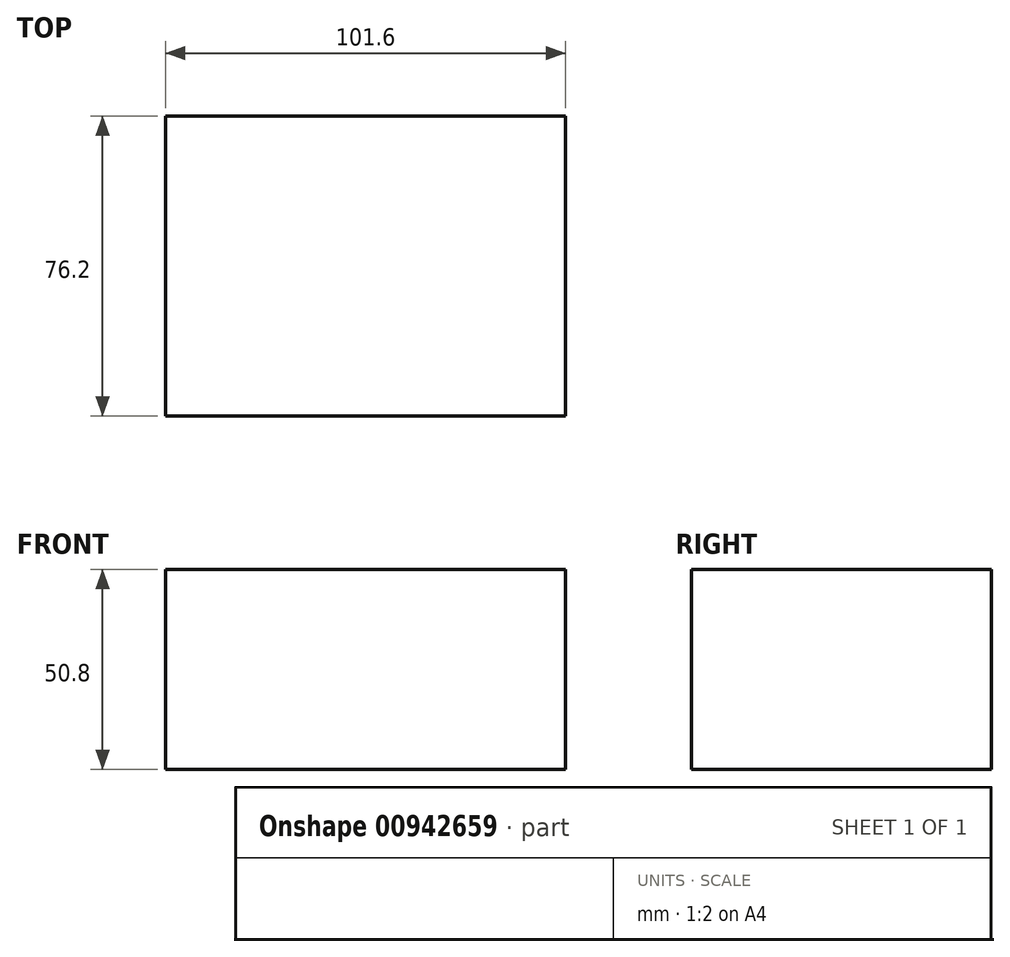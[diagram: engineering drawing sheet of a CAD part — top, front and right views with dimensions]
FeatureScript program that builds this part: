
annotation { "Feature Type Name" : "Feature", "Feature Type Description" : "" }
export const myFeature = defineFeature(function(context is Context, id is Id, definition is map)
    precondition{}
    {
        {
            var Q0;
            Q0=qCreatedBy(makeId("Front.planeOp"),FACE);
            var sketch = newSketch(context, id + "F0", { "sketchPlane" : qUnion([Q0])});
            skLineSegment(sketch, "E0.bottom", {"start": v(0, 0) * mm, "end": v(101.6, 0) * mm});
            skLineSegment(sketch, "E0.top", {"start": v(0, 50.8) * mm, "end": v(101.6, 50.8) * mm});
            skLineSegment(sketch, "E0.left", {"start": v(0, 0) * mm, "end": v(0, 50.8) * mm});
            skLineSegment(sketch, "E0.right", {"start": v(101.6, 0) * mm, "end": v(101.6, 50.8) * mm});
            skSolve(sketch);
        }
        {
            var Q0;
            Q0 = qSketchRegion(id + "F0", true);
            extrude(context, id + "F1", {"entities" : qUnion([Q0]), "depth" : 76.2 * mm, "offsetDistance" : 25.4 * mm});
        }
    });
